# Revit family: Accessories-Teknion-JNAUOD-Undermount_Personal_Storage-R2018
name_source: partatom
category: Furniture
revit_build: Autodesk Revit 2018 (Build: 20190510_1515(x64)
units: mm (PartAtom-declared; Revit-internal decimal feet)

## family parameters
Always vertical = Yes
Cut with Voids When Loaded = No
OmniClass Number = 23.40.20.00
OmniClass Title = General Furniture and Specialties
Room Calculation Point = No
Shared = Yes
Work Plane-Based = No

## types (2) — shared parameters
Assembly Code = E2020200
Manufacturer = Teknion
Manufacturer Fax = 416.661.4586
Part Number = JNAUOD
Product Documentation Link = https://www.teknion.com
Product Line = Expansion Cityline
Product Page URL = https://www.teknion.com
Series = Expansion Cityline
Sustainability Data = https://www.teknion.com
URL = www.teknion.com
Unit Weight URL = http://www.teknion.com
Warranty = http://www.teknion.com

## per-type parameters (varying)
| type | Cutout | Cutouts | Description | Model | Standard |
| Standard Mounting Style | 1 " | No | Undermount Personal Storage, Standard Mounting Style, 17 Height, 3 Width, 16 Depth | JNAUODS170716 | Yes |
| Navigate Frame Recessed Mounting Style | 9 " | Yes | Undermount Personal Storage, Navigate Frame Recessed Mounting Style, 17 Height, 3 Width, 16 Depth | JNAUODN170716 | No |

## geometry (parser evidence)
native form markers: Sweep x2
no freeform markers — native parametric forms only
